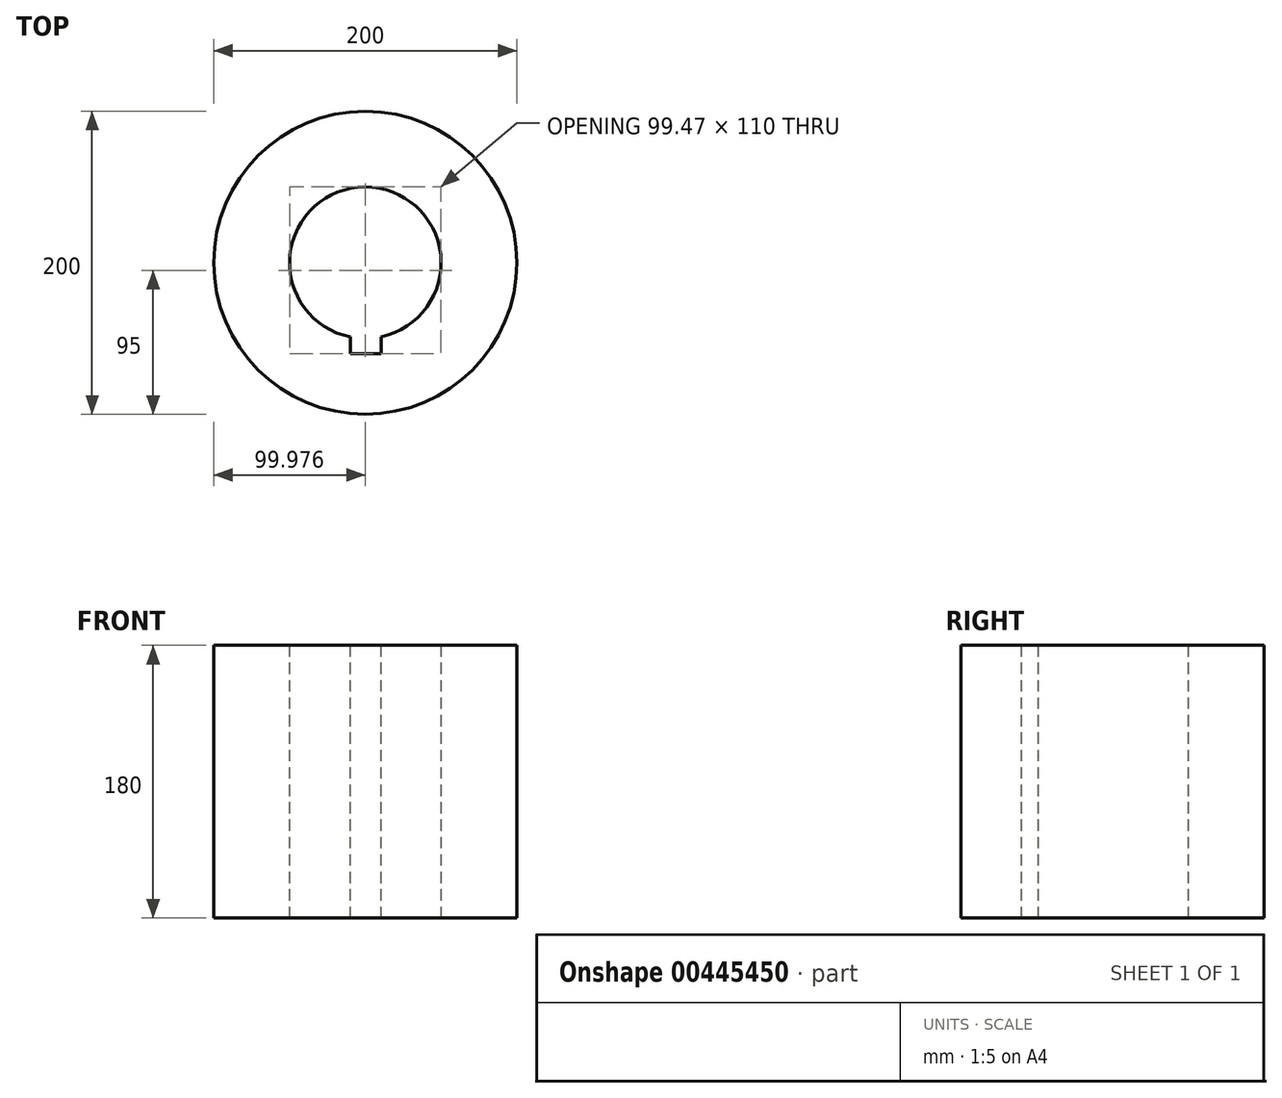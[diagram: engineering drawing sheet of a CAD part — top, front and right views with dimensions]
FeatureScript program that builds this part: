
annotation { "Feature Type Name" : "Feature", "Feature Type Description" : "" }
export const myFeature = defineFeature(function(context is Context, id is Id, definition is map)
    precondition{}
    {
        {
            var Q0;
            Q0=qCreatedBy(makeId("Top.planeOp"),FACE);
            var sketch = newSketch(context, id + "F0", { "sketchPlane" : qUnion([Q0])});
            skCircle(sketch, "E0", {"center": v(0, 0) * mm, "radius": 100 * mm});
            skSolve(sketch);
        }
        {
            var Q0;
            Q0 = qSketchRegion(id + "F0", true);
            extrude(context, id + "F1", {"entities" : qUnion([Q0]), "depth" : 180 * mm});
        }
        {
            var Q0;
            Q0=makeQuery(id+"F1.opExtrude","CAP_FACE",FACE,{"disambiguationData":[OSD([sQuery(id+"F0.wireOp",EDGE,"E0")])],"isStart":false});
            var sketch = newSketch(context, id + "F2", { "sketchPlane" : qUnion([Q0])});
            skCircle(sketch, "E1", {"center": v(0, 0) * mm, "radius": 50 * mm});
            skSolve(sketch);
        }
        {
            var Q0;
            Q0 = qSketchRegion(id + "F2", true);
            extrude(context, id + "F3", {"entities" : qUnion([Q0]), "operationType" : NewBodyOperationType.REMOVE, "endBound" : BoundingType.THROUGH_ALL, "oppositeDirection" : true, "depth" : 25 * mm});
        }
        {
            var Q0;
            Q0=makeQuery(id+"F1.opExtrude","CAP_FACE",FACE,{"disambiguationData":[OSD([sQuery(id+"F0.wireOp",EDGE,"E0")])],"isStart":false});
            var sketch = newSketch(context, id + "F4", { "sketchPlane" : qUnion([Q0])});
            skLineSegment(sketch, "E2.bottom", {"start": v(-10, -40.38) * mm, "end": v(10.45, -40.38) * mm});
            skLineSegment(sketch, "E2.top", {"start": v(-10, -60) * mm, "end": v(10.45, -60) * mm});
            skLineSegment(sketch, "E2.left", {"start": v(-10, -40.38) * mm, "end": v(-10, -60) * mm});
            skLineSegment(sketch, "E2.right", {"start": v(10.45, -40.38) * mm, "end": v(10.45, -60) * mm});
            skSolve(sketch);
        }
        {
            var Q0;
            Q0 = qSketchRegion(id + "F4", true);
            extrude(context, id + "F5", {"entities" : qUnion([Q0]), "operationType" : NewBodyOperationType.REMOVE, "endBound" : BoundingType.THROUGH_ALL, "oppositeDirection" : true, "depth" : 25 * mm});
        }
    });
